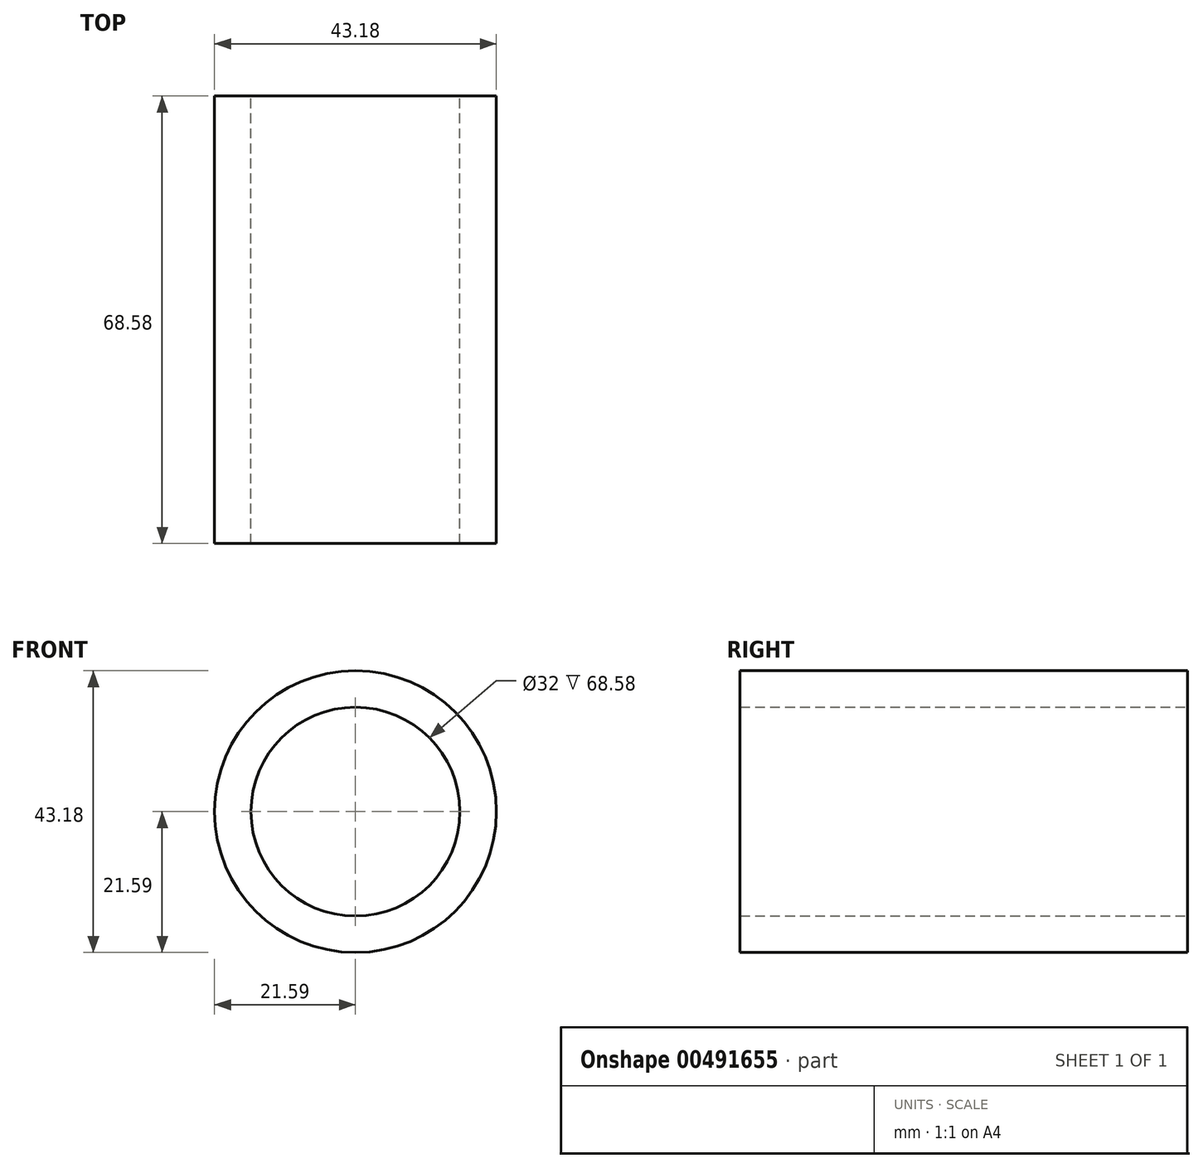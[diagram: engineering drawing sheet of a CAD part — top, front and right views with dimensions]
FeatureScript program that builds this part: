
annotation { "Feature Type Name" : "Feature", "Feature Type Description" : "" }
export const myFeature = defineFeature(function(context is Context, id is Id, definition is map)
    precondition{}
    {
        {
            var Q0;
            Q0=qCreatedBy(makeId("Front.planeOp"),FACE);
            var sketch = newSketch(context, id + "F0", { "sketchPlane" : qUnion([Q0])});
            skCircle(sketch, "E0", {"center": v(0, 0) * mm, "radius": 21.59 * mm});
            skCircle(sketch, "E1", {"center": v(0, 0) * mm, "radius": 16 * mm});
            skSolve(sketch);
        }
        {
            var Q0;
            Q0=makeQuery(id+"F0.imprint","IMPRINT",FACE,{"disambiguationData":[TD([[makeQuery(id+"F0.imprint","IMPRINT",EDGE,{"derivedFrom":sQuery(id+"F0.wireOp",EDGE,"E0")}),1.0]])]});
            var Q1;
            Q1=sQuery(id+"F0.wireOp",EDGE,"E1");
            var Q2;
            Q2=sQuery(id+"F0.wireOp",EDGE,"E0");
            extrude(context, id + "F1", {"entities" : qUnion([Q0]), "surfaceEntities" : qUnion([Q1, Q2]), "depth" : 68.58 * mm});
        }
    });
